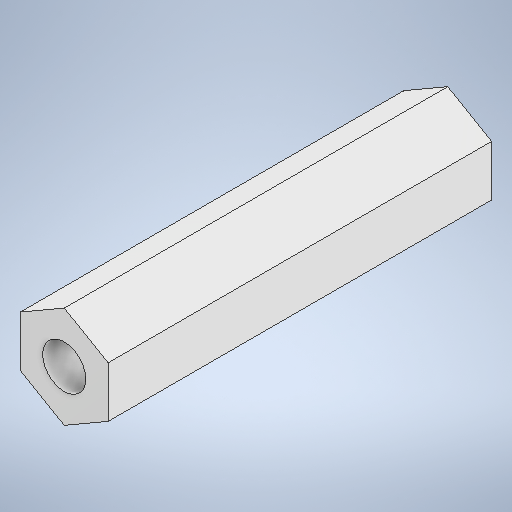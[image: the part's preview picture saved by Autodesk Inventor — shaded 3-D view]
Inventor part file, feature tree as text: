
AUTODESK INVENTOR PART (.ipt)
format: ipt  version: 2025.3 (Build 293356000, 356)  size: 219,136 bytes
history: native  units: mm
features: other x1, extrude x1
ambient origin geometry x8: Origin, YZ Plane, XZ Plane, XY Plane, X Axis, Y Axis, Z Axis, Center Point
bodies: Body1 (feature_tree)
feature tree (2):
  other  "ソリッド1"
  extrude  "押し出し1"  Depth=5.5mm
